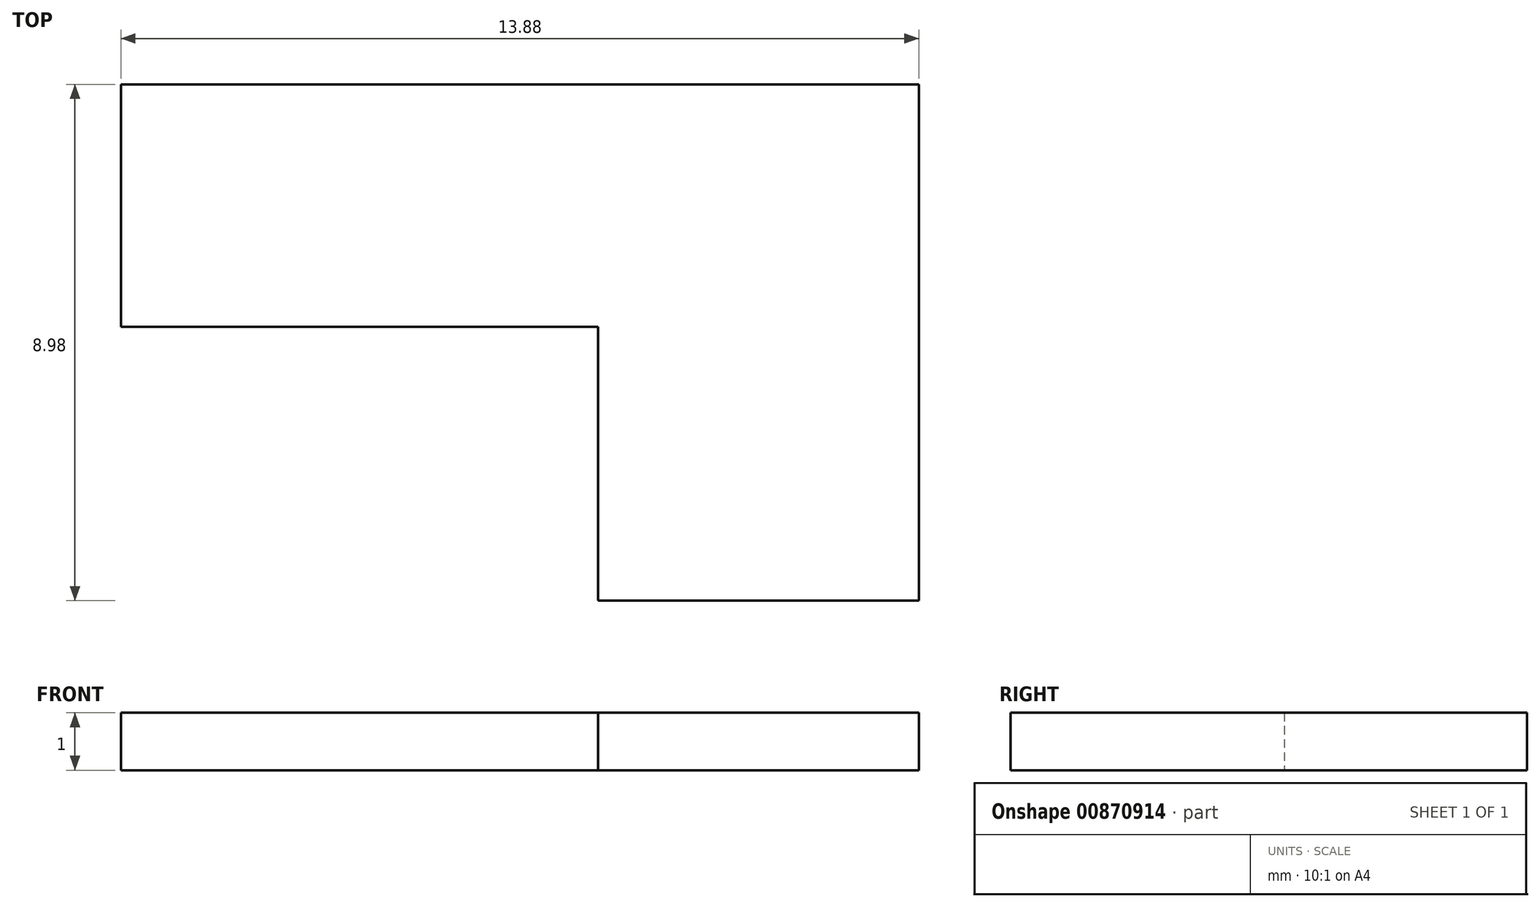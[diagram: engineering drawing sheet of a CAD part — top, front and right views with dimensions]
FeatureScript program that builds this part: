
annotation { "Feature Type Name" : "Feature", "Feature Type Description" : "" }
export const myFeature = defineFeature(function(context is Context, id is Id, definition is map)
    precondition{}
    {
        {
            var Q0;
            Q0=qCreatedBy(makeId("Top.planeOp"),FACE);
            var sketch = newSketch(context, id + "F0", { "sketchPlane" : qUnion([Q0])});
            skLineSegment(sketch, "E0", {"start": v(-8.3, 4.22) * mm, "end": v(5.58, 4.22) * mm});
            skLineSegment(sketch, "E1", {"start": v(5.58, 4.22) * mm, "end": v(5.58, -4.76) * mm});
            skLineSegment(sketch, "E2", {"start": v(5.58, -4.76) * mm, "end": v(0, -4.76) * mm});
            skLineSegment(sketch, "E3", {"start": v(0, -4.76) * mm, "end": v(0, 0) * mm});
            skLineSegment(sketch, "E4", {"start": v(-8.3, 0) * mm, "end": v(-8.3, 4.22) * mm});
            skLineSegment(sketch, "E5", {"start": v(-8.3, 0) * mm, "end": v(0, 0) * mm});
            skSolve(sketch);
        }
        {
            var Q0;
            Q0 = qSketchRegion(id + "F0", true);
            extrude(context, id + "F1", {"entities" : qUnion([Q0]), "depth" : 1 * mm, "offsetDistance" : 25.4 * mm});
        }
    });
